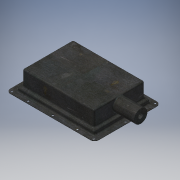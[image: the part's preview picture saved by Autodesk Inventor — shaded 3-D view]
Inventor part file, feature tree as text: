
AUTODESK INVENTOR PART (.ipt)
format: ipt  version: 2018 (Build 220112000, 112)  size: 487,424 bytes
history: native  units: mm
features: fillet x5, extrude x4, sketch x4, hole x1, projected_geometry x1
ambient origin geometry x8: Origin, YZ Plane, XZ Plane, XY Plane, X Axis, Y Axis, Z Axis, Center Point
bodies: Body1 (feature_tree)
feature tree (15):
  extrude  "Extrusion5"  Depth=162.0mm
  extrude  "Extrusion6"  Depth=188.0mm
  extrude  "Extrusion7"  Depth=10.0mm TaperAngle=0.0deg
  fillet  "Rundung1"  Radius=175.0mm
  fillet  "Rundung2"  Radius=124.0mm
  fillet  "Rundung3"  Radius=38.0mm
  fillet  "Rundung4"  Radius=10.0mm
  extrude  "Extrusion8"  Depth=2.0mm
  fillet  "Rundung5"  Radius=4.0mm
  hole  "Bohrung1"  [1 undecoded]
  sketch  "Skizze1"  dims[d17=216.0mm d18=162.0mm]
  sketch  "Skizze6"  dims[d21=1.0mm d22=0.0mm d23=188.0mm]
  sketch  "Skizze7"  dims[d24=136.0mm d25=10.0mm d26=0.0mm d27=175.0mm d28=124.0mm d29=38.0mm d30=0.0mm d31=10.0mm]
  sketch  "Skizze8"  dims[d32=4.0mm d33=4.0mm d34=4.0mm d35=4.0mm d36=32.5mm d37=52.0mm d38=0.0mm d39=2.0mm d43=10.0mm d44=10.0mm d45=11.445mm d46=5.0mm d47=4.0mm d48=2.0mm d49=90.0deg d50=8.0mm d51=20.594885mm]
  projected_geometry  "Projizierte Kontur4"
note: 1 required parameter value undecoded (feature->parameter linkage not recoverable at this tier; creation-order binding heuristic only, values carry confidence <= 0.55)
